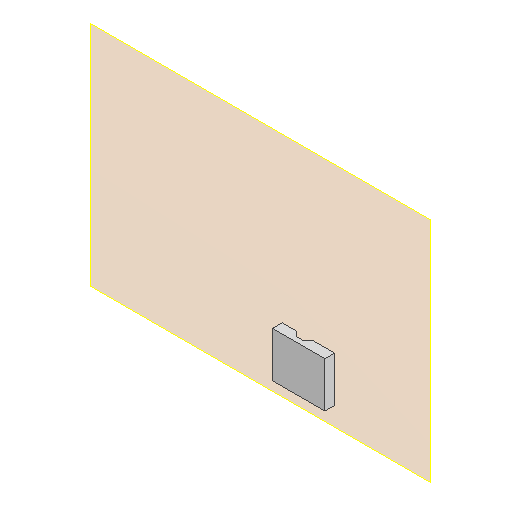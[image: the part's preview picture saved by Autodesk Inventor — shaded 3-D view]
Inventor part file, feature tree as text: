
AUTODESK INVENTOR PART (.ipt)
format: ipt  version: 2022 (Build 260153000, 153)  size: 132,608 bytes
history: native  units: mm
features: other x3, extrude x2, sketch x2, plane x1, chamfer x1, reference x1, projected_geometry x1
ambient origin geometry x8: Origin, YZ Plane, XZ Plane, XY Plane, X Axis, Y Axis, Z Axis, Center Point
bodies: Volumenkörper1 (feature_tree)
feature tree (11):
  plane  "Arbeitsebene1"
  extrude  "Extrusion1"  Depth=4.0mm TaperAngle=0.0deg
  extrude  "Extrusion2"  Depth=1.8mm TaperAngle=45.0deg
  chamfer  "Fase1"  [1 undecoded]
  sketch  "Skizze1"  dims[d0=0.5mm d3=4.0mm d4=0.0mm]
  reference  "Referenz1"
  sketch  "Skizze2"  dims[d5=2.0mm d6=0.0mm d7=1.8mm d8=2.0mm d9=45.0deg]
  projected_geometry  "Projizierte Kontur1"
  other  "<userpath>\Documents\GitHub\Guinardia\INVENTOR\Assembly_Guinardia_V1.iam"
  other  "Assembly_Guinardia_V1.iam"
  other  "10_Wellplate_base_v1:1"
note: 1 required parameter value undecoded (feature->parameter linkage not recoverable at this tier; creation-order binding heuristic only, values carry confidence <= 0.55)
